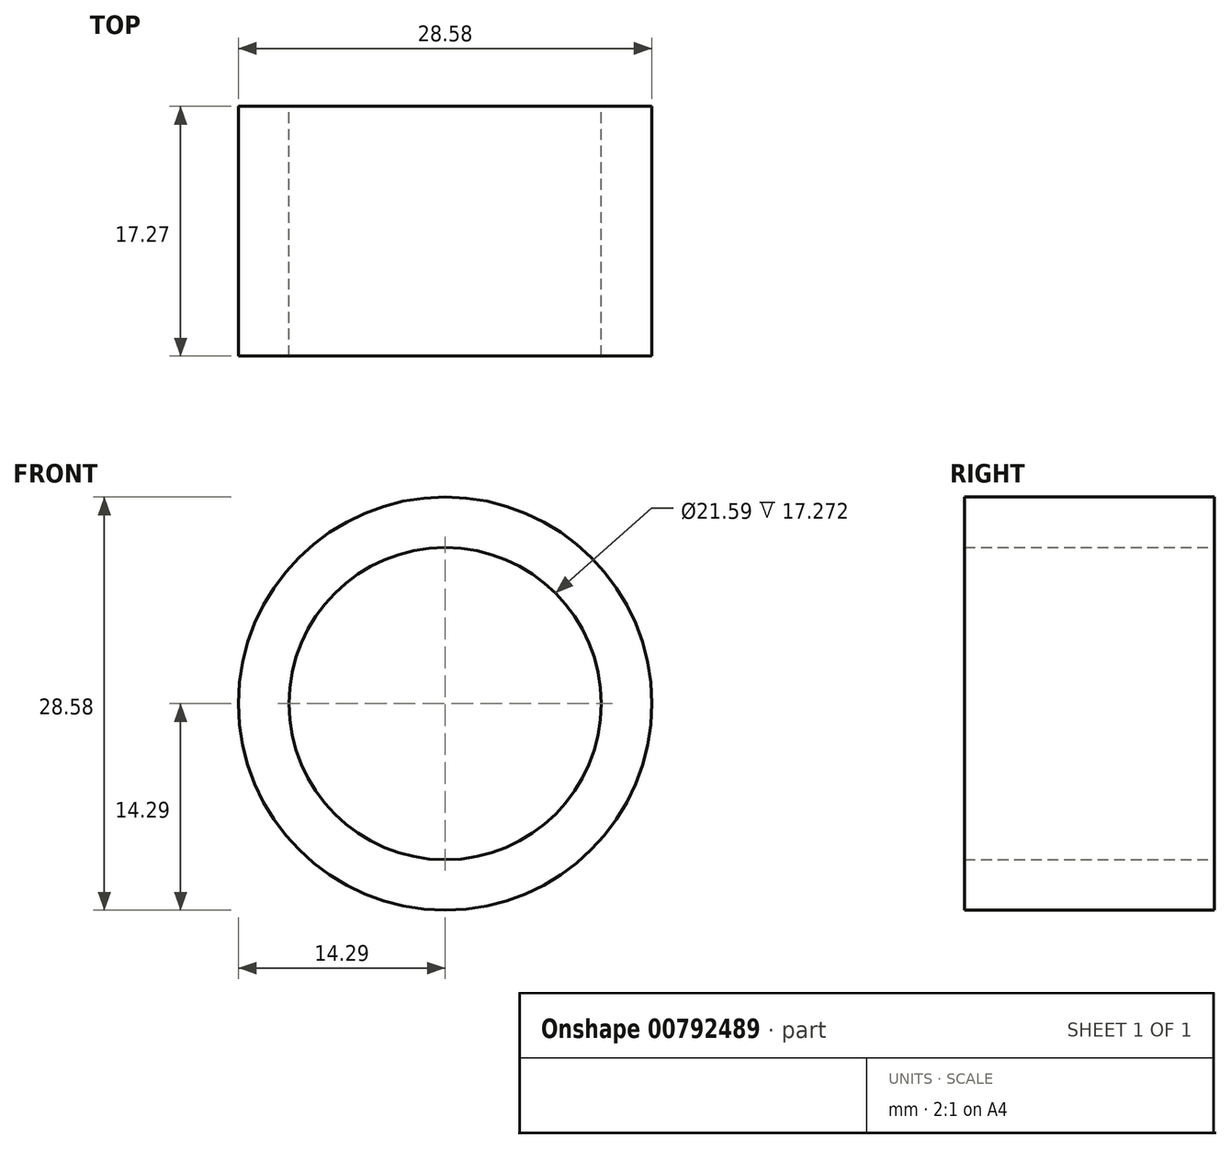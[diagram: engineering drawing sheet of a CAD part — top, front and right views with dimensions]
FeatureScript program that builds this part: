
annotation { "Feature Type Name" : "Feature", "Feature Type Description" : "" }
export const myFeature = defineFeature(function(context is Context, id is Id, definition is map)
    precondition{}
    {
        {
            var Q0;
            Q0=qCreatedBy(makeId("Front.planeOp"),FACE);
            var sketch = newSketch(context, id + "F0", { "sketchPlane" : qUnion([Q0])});
            skCircle(sketch, "E0", {"center": v(0, 0) * mm, "radius": 14.29 * mm});
            skCircle(sketch, "E1", {"center": v(0, 0) * mm, "radius": 10.8 * mm});
            skSolve(sketch);
        }
        {
            var Q0;
            Q0=qSketchRegion(id+"F0",true);
            extrude(context, id + "F1", {"entities" : qUnion([Q0]), "depth" : 17.27 * mm, "offsetDistance" : 25.4 * mm});
        }
    });
